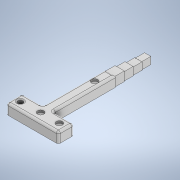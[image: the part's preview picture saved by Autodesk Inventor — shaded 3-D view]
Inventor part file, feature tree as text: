
AUTODESK INVENTOR PART (.ipt)
format: ipt  version: 2022 (Build 260153000, 153)  size: 221,184 bytes
history: native  units: mm
features: extrude x7, sketch x7, fillet x2
ambient origin geometry x8: Origin, YZ Plane, XZ Plane, XY Plane, X Axis, Y Axis, Z Axis, Center Point
bodies: Solid1 (feature_tree)
feature tree (16):
  extrude  "Extrusion1"  TaperAngle=0.0deg  [1 undecoded]
  extrude  "Extrusion5"  Depth=20.0mm
  extrude  "Extrusion2"  Depth=15.0mm
  extrude  "Extrusion3"  Depth=7.92mm
  extrude  "Extrusion4"  Depth=9.0mm TaperAngle=0.0deg
  fillet  "Fillet1"  Radius=7.0mm
  extrude  "Extrusion6"  Depth=0.46mm
  fillet  "Fillet2"  Radius=0.46mm
  extrude  "Extrusion7"  Depth=6.04mm
  sketch  "Sketch1"  dims[d0=10.0mm d2=0.0mm]
  sketch  "Sketch2"  dims[d5=10.0mm d6=0.0mm d7=12.0mm d8=20.0mm]
  sketch  "Sketch3"  dims[d9=20.0mm d10=15.0mm]
  sketch  "Sketch4"  dims[d11=75.0mm d12=7.92mm]
  sketch  "Sketch5"  dims[d13=7.92mm d16=9.0mm d17=0.0mm d19=7.0mm]
  sketch  "Sketch6"  dims[d20=7.0mm d21=0.46mm d22=0.46mm]
  sketch  "Sketch7"  dims[d23=9.0mm d24=0.0mm d25=6.04mm d26=6.84mm d27=0.48mm d28=0.48mm d29=9.0mm d30=0.0mm d31=10.0mm d32=8.9mm d33=8.9mm d34=0.5mm d35=9.0mm d36=0.0mm d37=0.49mm d38=0.49mm d39=2.0mm d40=5.0mm d41=7.5mm d42=7.5mm d43=6.0mm d44=9.0mm d45=0.0mm d46=1.0mm d47=6.0mm d48=5.0mm d49=60.0mm d50=5.0mm d51=5.0mm d52=18.0mm d53=2.0mm d54=0.0mm]
note: 1 required parameter value undecoded (feature->parameter linkage not recoverable at this tier; creation-order binding heuristic only, values carry confidence <= 0.55)
